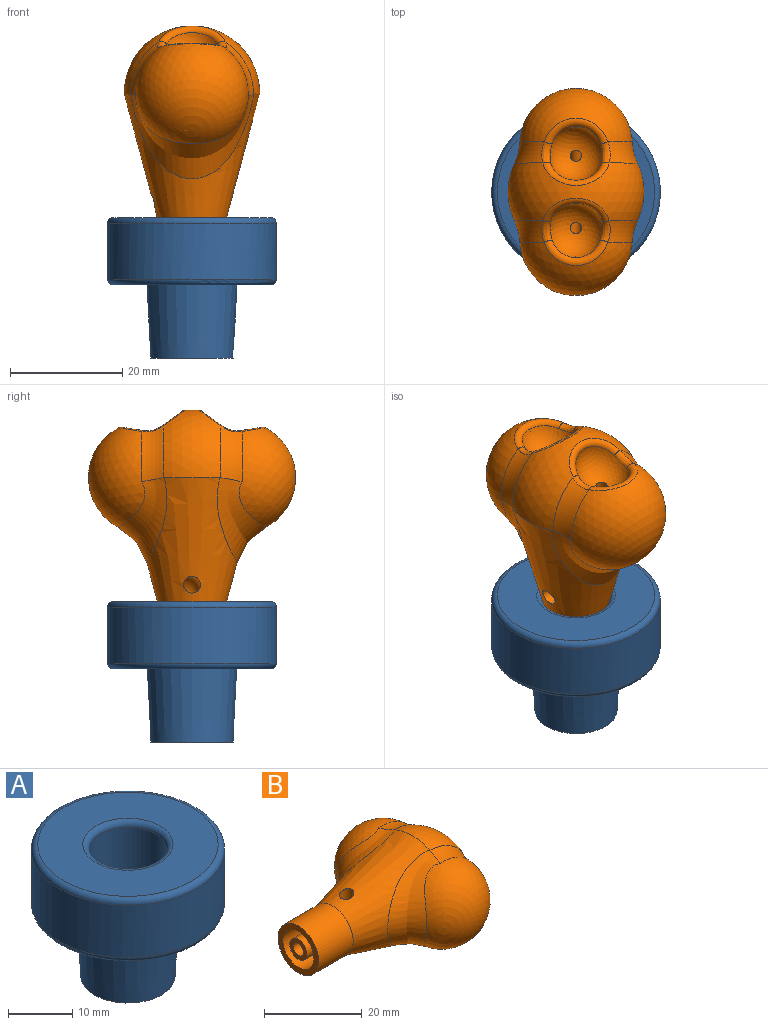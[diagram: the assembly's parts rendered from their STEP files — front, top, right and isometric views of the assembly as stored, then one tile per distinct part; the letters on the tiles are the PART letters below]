
ASSEMBLY  parts=2 mates=1
PART A: 11 faces, bbox 32.5x32.5x25 mm
  f0: cylinder r=6mm len=24mm, axis (0,0,-1), area 904.8mm2, adj f1,f10
  f1: plane 14.64x14.64mm, normal (0,0,-1), area 55.2mm2, adj f0,f2
  f2: cone r=8mm half-angle=3deg, axis (0,0,1), area 1146.3mm2, adj f1,f3
  f3: plane 26x26mm, normal (0,0,-1), area 302.7mm2, adj f2,f4
  f4: cylinder r=13mm len=26mm, axis (0,0,-1), area 816.8mm2, adj f3,f5
  f5: plane 28x28mm, normal (0,0,-1), area 84.8mm2, adj f4,f8
  f6: cylinder r=15mm len=30mm, axis (0,0,-1), area 942.5mm2, adj f8,f9
  f7: plane 28x28mm, normal (0,0,1), area 461.8mm2, adj f9,f10
  f8: torus R=14mm, axis (0,0,1), area 144.5mm2, adj f5,f6
  f9: torus R=14mm, axis (0,0,-1), area 144.5mm2, adj f6,f7
  f10: torus R=7mm, axis (0,0,-1), area 62.8mm2, adj f0,f7
PART B: 32 faces, bbox 48.2x37.2x28.2 mm
  f0: plane 9.28x4.78mm, normal (-1,0,0), area 18.8mm2, adj f24,f25,f26,f28
  f1: plane 9.28x4.78mm, normal (-1,0,0), area 18.8mm2, adj f24,f25,f26,f28
  f2: sphere r=12.08mm, area 314.2mm2, adj f5,f10,f11,f12,f13,f14,f19,f20
  f3: sphere r=10mm, area 479mm2, adj f10,f11,f17,f20
  f4: sphere r=10mm, area 501.6mm2, adj f12,f13,f16,f21
  f5: cone r=5.9mm half-angle=15deg, axis (1,0,0), area 725.6mm2, adj f2,f6,f10,f12,f31
  f6: cylinder r=5.9mm len=11.8mm, axis (-1,0,0), area 370.7mm2, adj f5,f7
  f7: plane 11.8x11.8mm, normal (-1,0,0), area 45.7mm2, adj f6,f24
  f8: sphere r=5mm, area 121.2mm2, adj f14,f15,f16,f22,f26
  f9: sphere r=5mm, area 121.1mm2, adj f17,f18,f19,f23,f25
  f10: bspline ~22.65x17.9mm, area 205.8mm2, adj f2,f3,f5,f11,f20
  f11: torus R=19.98mm, axis (0,1,0), area 40.2mm2, adj f2,f3,f10,f18
  f12: bspline ~22.67x17.85mm, area 205.8mm2, adj f2,f4,f5,f13,f21
  f13: torus R=19.98mm, axis (0,1,0), area 40.2mm2, adj f2,f4,f12,f15
  f14: torus R=5.48mm, axis (0.82,-0.57,0), area 24.1mm2, adj f2,f8,f15,f22
  f15: bspline ~5.15x2.22mm, area 6.5mm2, adj f8,f13,f14,f16
  f16: torus R=5.33mm, axis (0.99,0.15,0), area 22.7mm2, adj f4,f8,f15,f22
  f17: torus R=5.33mm, axis (-0.99,0.15,0), area 22.7mm2, adj f3,f9,f18,f23
  f18: bspline ~5.77x2.36mm, area 6.5mm2, adj f9,f11,f17,f19
  f19: torus R=5.48mm, axis (0.82,0.57,0), area 24.1mm2, adj f2,f9,f18,f23
  f20: torus R=19.98mm, axis (0,1,0), area 40.2mm2, adj f2,f3,f10,f23
  f21: torus R=19.98mm, axis (0,1,0), area 40.2mm2, adj f2,f4,f12,f22
  f22: bspline ~5.77x2.36mm, area 6.5mm2, adj f8,f14,f16,f21
  f23: bspline ~5.77x2.36mm, area 6.5mm2, adj f9,f17,f19,f20
  f24: cylinder r=4.5mm len=10mm, axis (-1,0,0), area 282.7mm2, adj f0,f1,f7
  f25: bspline ~28.06x4.92mm, area 177.1mm2, adj f0,f1,f9
  f26: bspline ~28.06x4.92mm, area 177.1mm2, adj f0,f1,f8
  f27: cylinder r=1.5mm len=11mm, axis (1,0,0), area 103.7mm2, adj f29,f30
  f28: cylinder r=2.5mm len=10mm, axis (1,0,0), area 157.1mm2, adj f0,f1,f29
  f29: plane 5x5mm, normal (-1,0,0), area 12.6mm2, adj f27,f28
  f30: torus R=3mm, axis (0,-1,0), area 44.4mm2, adj f27,f31
  f31: cylinder r=1.5mm len=4.38mm, axis (0,0,1), area 36.7mm2, adj f5,f30
PLACE A t=(6.8,0,0)mm
PLACE B rot(axis=(0,-1,0),90deg) t=(6.8,0,36)mm
MATE revolute B.f5 <-> A.f0  axis (0,0,-1) through (6.8,0,14)mm
